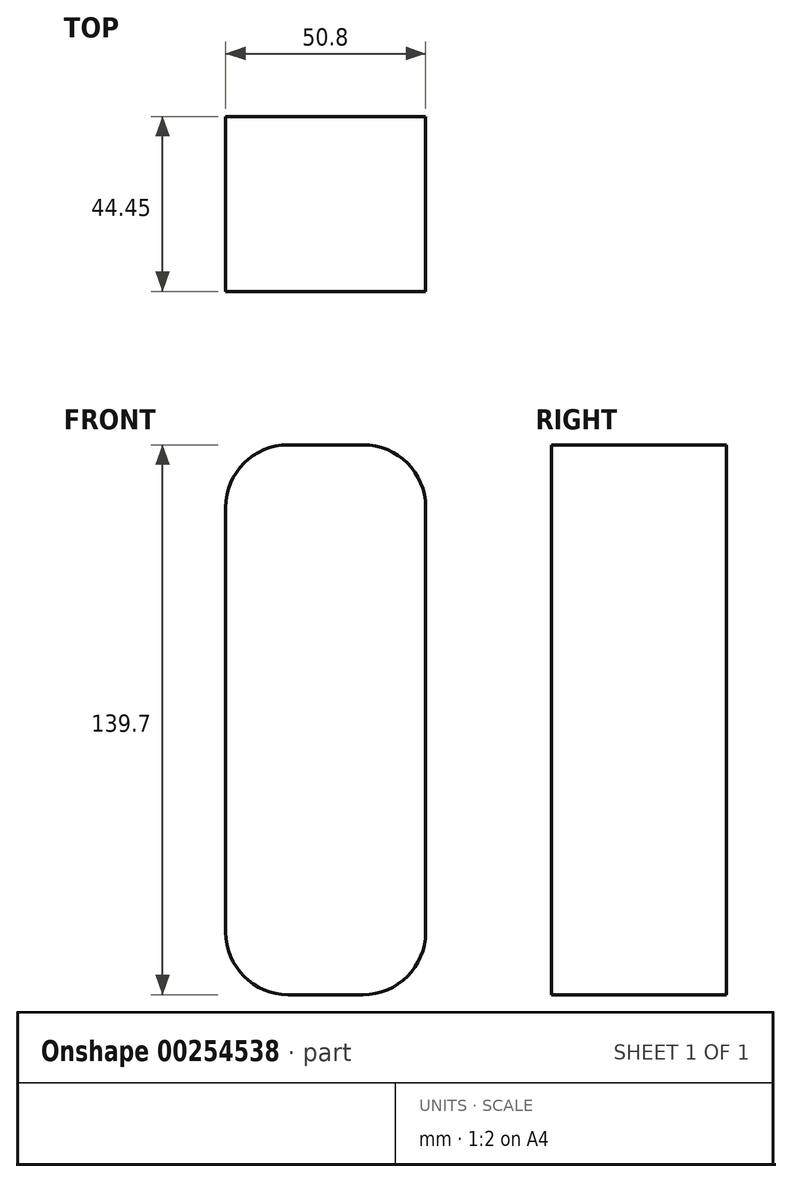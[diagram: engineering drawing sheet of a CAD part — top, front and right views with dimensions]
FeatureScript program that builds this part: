
annotation { "Feature Type Name" : "Feature", "Feature Type Description" : "" }
export const myFeature = defineFeature(function(context is Context, id is Id, definition is map)
    precondition{}
    {
        {
            var Q0;
            Q0=qCreatedBy(makeId("Front.planeOp"),FACE);
            var sketch = newSketch(context, id + "F0", { "sketchPlane" : qUnion([Q0])});
            skLineSegment(sketch, "E0.bottom", {"start": v(9.52, 69.85) * mm, "end": v(-9.53, 69.85) * mm});
            skLineSegment(sketch, "E0.top", {"start": v(9.53, -69.85) * mm, "end": v(-9.52, -69.85) * mm});
            skLineSegment(sketch, "E0.left", {"start": v(25.4, 53.98) * mm, "end": v(25.4, -53.98) * mm});
            skLineSegment(sketch, "E0.right", {"start": v(-25.4, 53.98) * mm, "end": v(-25.4, -53.98) * mm});
            skPoint(sketch, "E0.middle", {"position": v(0, 0) * mm});
            skPoint(sketch, "E1.visualSharp", {"position": v(-25.4, 69.85) * mm});
            skArc(sketch, "E1.filletArc", {"start": v(-9.53, 69.85) * mm, "mid": v(-20.75, 65.2) * mm, "end": v(-25.4, 53.98) * mm});
            skPoint(sketch, "E2.visualSharp", {"position": v(25.4, 69.85) * mm});
            skArc(sketch, "E2.filletArc", {"start": v(25.4, 53.98) * mm, "mid": v(20.75, 65.2) * mm, "end": v(9.52, 69.85) * mm});
            skPoint(sketch, "E3.visualSharp", {"position": v(25.4, -69.85) * mm});
            skArc(sketch, "E3.filletArc", {"start": v(9.53, -69.85) * mm, "mid": v(20.75, -65.2) * mm, "end": v(25.4, -53.98) * mm});
            skPoint(sketch, "E4.visualSharp", {"position": v(-25.4, -69.85) * mm});
            skArc(sketch, "E4.filletArc", {"start": v(-25.4, -53.98) * mm, "mid": v(-20.75, -65.2) * mm, "end": v(-9.52, -69.85) * mm});
            skSolve(sketch);
        }
        {
            var Q0;
            Q0 = qSketchRegion(id + "F0", true);
            extrude(context, id + "F1", {"entities" : qUnion([Q0]), "depth" : 44.45 * mm});
        }
    });
